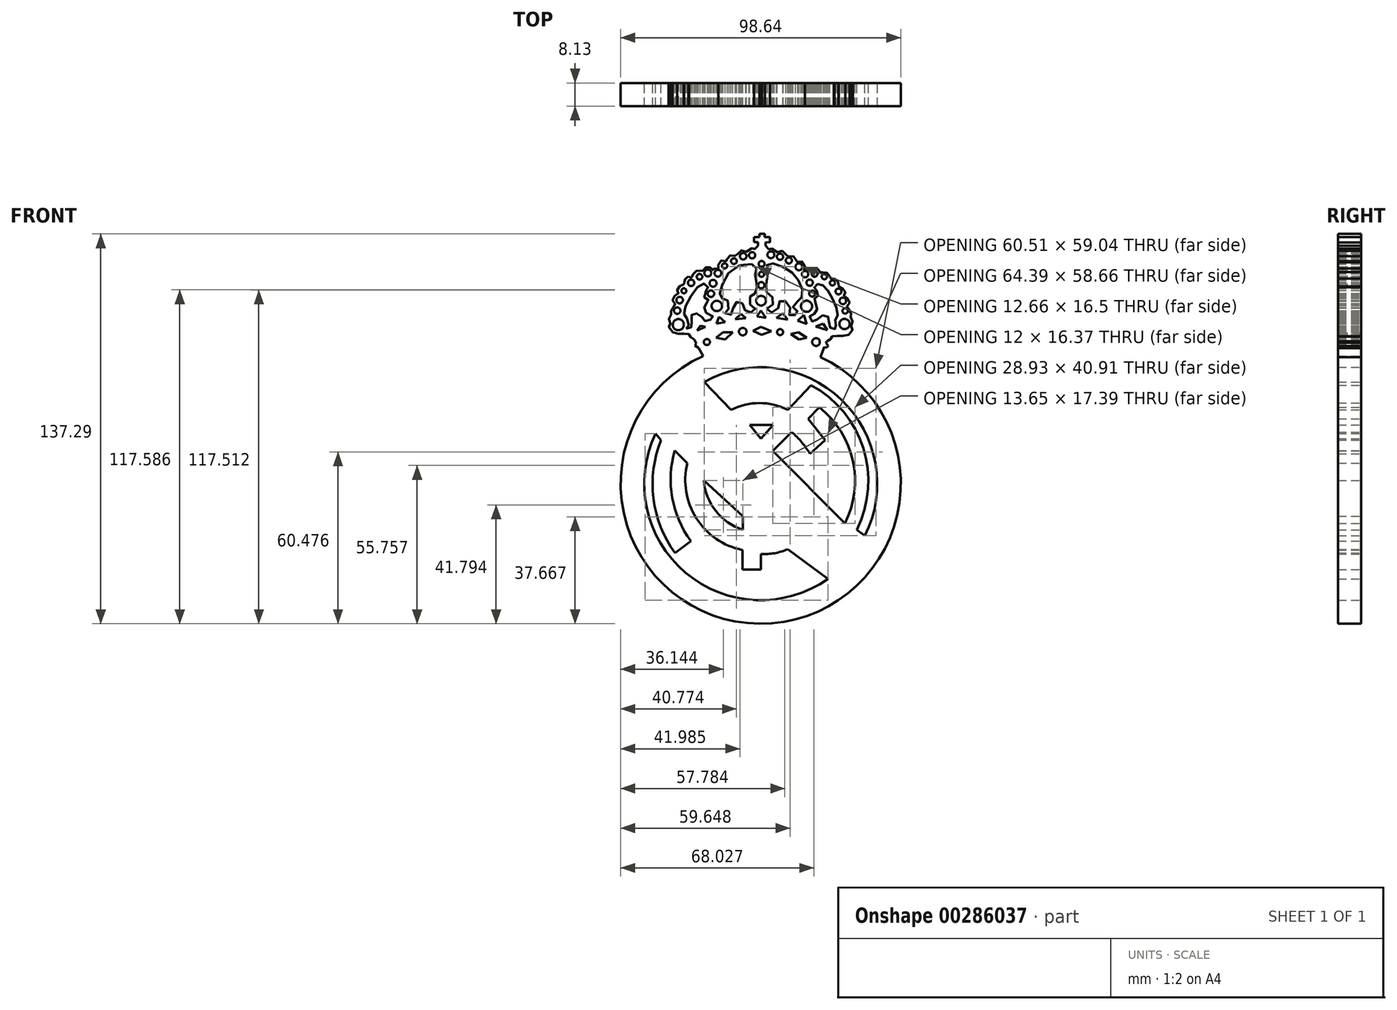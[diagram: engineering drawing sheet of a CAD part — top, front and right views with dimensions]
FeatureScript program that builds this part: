
annotation { "Feature Type Name" : "Feature", "Feature Type Description" : "" }
export const myFeature = defineFeature(function(context is Context, id is Id, definition is map)
    precondition{}
    {
        {
            var Q0;
            Q0=qCreatedBy(makeId("Front.planeOp"),FACE);
            var sketch = newSketch(context, id + "F0", { "sketchPlane" : qUnion([Q0])});
            skCircle(sketch, "E0", {"center": v(0, -1.17) * mm, "radius": 49.32 * mm});
            skCircle(sketch, "E1", {"center": v(0, -1.17) * mm, "radius": 41.02 * mm});
            skArc(sketch, "E2", {"start": v(-18.95, 33.67) * mm, "mid": v(-37.34, 6.45) * mm, "end": v(-30.16, -25.6) * mm});
            skArc(sketch, "E3", {"start": v(-19.8, 27.48) * mm, "mid": v(-31.53, 3.97) * mm, "end": v(-24.63, -21.38) * mm});
            skLineSegment(sketch, "E4", {"start": v(-19.8, 27.48) * mm, "end": v(-14.73, 21.41) * mm});
            skLineSegment(sketch, "E5", {"start": v(-18.95, 33.67) * mm, "end": v(-10.43, 24.82) * mm});
            skArc(sketch, "E6", {"start": v(-14.73, 21.41) * mm, "mid": v(-26.18, -4.34) * mm, "end": v(-6.47, -24.5) * mm});
            skLineSegment(sketch, "E7", {"start": v(-6.47, -24.5) * mm, "end": v(-6.47, -31.38) * mm});
            skLineSegment(sketch, "E8", {"start": v(-6.47, -31.38) * mm, "end": v(0, -31.38) * mm});
            skLineSegment(sketch, "E9", {"start": v(0, -31.38) * mm, "end": v(0, -25.92) * mm});
            skArc(sketch, "E10", {"start": v(0, -25.92) * mm, "mid": v(10.77, -23.7) * mm, "end": v(19, -16.42) * mm});
            skLineSegment(sketch, "E11", {"start": v(19, -16.42) * mm, "end": v(15.77, -12.98) * mm});
            skArc(sketch, "E12", {"start": v(0, -19.42) * mm, "mid": v(8.55, -17.84) * mm, "end": v(15.77, -12.98) * mm});
            skLineSegment(sketch, "E13", {"start": v(0, -19.42) * mm, "end": v(0, -13.17) * mm});
            skLineSegment(sketch, "E14", {"start": v(0, -13.17) * mm, "end": v(7.9, -13.17) * mm});
            skLineSegment(sketch, "E15", {"start": v(7.9, -13.17) * mm, "end": v(7.9, -8.88) * mm});
            skLineSegment(sketch, "E16", {"start": v(7.9, -8.88) * mm, "end": v(0, -8.88) * mm});
            skLineSegment(sketch, "E17", {"start": v(0, -8.88) * mm, "end": v(0, -3.61) * mm});
            skLineSegment(sketch, "E18", {"start": v(0, -3.61) * mm, "end": v(8.16, -3.61) * mm});
            skLineSegment(sketch, "E19", {"start": v(8.16, -3.61) * mm, "end": v(8.16, 0.94) * mm});
            skLineSegment(sketch, "E20", {"start": v(8.16, 0.94) * mm, "end": v(-6.35, 0.94) * mm});
            skLineSegment(sketch, "E21", {"start": v(-6.35, 0.94) * mm, "end": v(-6.35, -17.53) * mm});
            skArc(sketch, "E22", {"start": v(-11.49, 17.79) * mm, "mid": v(-19.81, -1.63) * mm, "end": v(-5.9, -17.53) * mm});
            skLineSegment(sketch, "E23", {"start": v(-11.49, 17.79) * mm, "end": v(0, 6.2) * mm});
            skLineSegment(sketch, "E24", {"start": v(0, 6.2) * mm, "end": v(10.89, 17) * mm});
            skArc(sketch, "E25", {"start": v(17.4, 9.33) * mm, "mid": v(14.45, 13.43) * mm, "end": v(10.89, 17) * mm});
            skLineSegment(sketch, "E26", {"start": v(17.4, 9.33) * mm, "end": v(22.73, 14.2) * mm});
            skLineSegment(sketch, "E27", {"start": v(22.73, 14.2) * mm, "end": v(16.74, 21.7) * mm});
            skLineSegment(sketch, "E28", {"start": v(16.74, 21.7) * mm, "end": v(20.65, 25.72) * mm});
            skLineSegment(sketch, "E29", {"start": v(-4.2, 19.87) * mm, "end": v(0, 14.73) * mm});
            skLineSegment(sketch, "E30", {"start": v(0, 14.73) * mm, "end": v(4.38, 19.54) * mm});
            skLineSegment(sketch, "E31", {"start": v(4.38, 19.54) * mm, "end": v(-3.94, 19.54) * mm});
            skArc(sketch, "E32", {"start": v(9.56, 24.82) * mm, "mid": v(-0.44, 27.23) * mm, "end": v(-10.43, 24.82) * mm});
            skLineSegment(sketch, "E33", {"start": v(9.56, 24.82) * mm, "end": v(17.72, 33.54) * mm});
            skArc(sketch, "E34", {"start": v(30.1, -23.34) * mm, "mid": v(36.99, 7.94) * mm, "end": v(17.72, 33.54) * mm});
            skLineSegment(sketch, "E35", {"start": v(30.1, -24) * mm, "end": v(26.4, -20.38) * mm});
            skLineSegment(sketch, "E36", {"start": v(30.1, -24) * mm, "end": v(30.1, -23.34) * mm});
            skArc(sketch, "E37", {"start": v(26.4, -20.38) * mm, "mid": v(32.95, 3.85) * mm, "end": v(20.65, 25.72) * mm});
            skLineSegment(sketch, "E38", {"start": v(-23.41, 49.61) * mm, "end": v(-20.3, 43.78) * mm});
            skArc(sketch, "E39", {"start": v(23.39, 49.61) * mm, "mid": v(-0.01, 54.78) * mm, "end": v(-23.41, 49.61) * mm});
            skLineSegment(sketch, "E40", {"start": v(23.39, 49.61) * mm, "end": v(21, 43.45) * mm});
            skCircle(sketch, "E41", {"center": v(-6.34, 52.39) * mm, "radius": 1.32 * mm});
            skCircle(sketch, "E42", {"center": v(6.84, 52.21) * mm, "radius": 1.06 * mm});
            skCircle(sketch, "E43", {"center": v(19.47, 48.72) * mm, "radius": 1.36 * mm});
            skCircle(sketch, "E44", {"center": v(-18.96, 48.72) * mm, "radius": 1.07 * mm});
            skLineSegment(sketch, "E45", {"start": v(-15.7, 50.27) * mm, "end": v(-13.28, 52.16) * mm});
            skLineSegment(sketch, "E46", {"start": v(-13.28, 52.16) * mm, "end": v(-9.81, 52.16) * mm});
            skLineSegment(sketch, "E47", {"start": v(-9.81, 52.16) * mm, "end": v(-12.48, 49.66) * mm});
            skLineSegment(sketch, "E48", {"start": v(-12.48, 49.66) * mm, "end": v(-15.7, 50.27) * mm});
            skLineSegment(sketch, "E49", {"start": v(-2.79, 52.65) * mm, "end": v(0, 54) * mm});
            skLineSegment(sketch, "E50", {"start": v(0, 54) * mm, "end": v(3.69, 52.55) * mm});
            skLineSegment(sketch, "E51", {"start": v(3.69, 52.55) * mm, "end": v(0.37, 51.28) * mm});
            skLineSegment(sketch, "E52", {"start": v(0.37, 51.28) * mm, "end": v(-2.79, 52.65) * mm});
            skLineSegment(sketch, "E53", {"start": v(10.66, 51.51) * mm, "end": v(13.3, 52.2) * mm});
            skLineSegment(sketch, "E54", {"start": v(13.3, 52.2) * mm, "end": v(16.15, 50.27) * mm});
            skLineSegment(sketch, "E55", {"start": v(16.15, 50.27) * mm, "end": v(13.51, 49.6) * mm});
            skLineSegment(sketch, "E56", {"start": v(13.51, 49.6) * mm, "end": v(10.66, 51.51) * mm});
            skLineSegment(sketch, "E57", {"start": v(21.74, 47.98) * mm, "end": v(22.72, 48.74) * mm});
            skLineSegment(sketch, "E58", {"start": v(22.72, 48.74) * mm, "end": v(23.77, 47.39) * mm});
            skLineSegment(sketch, "E59", {"start": v(23.77, 47.39) * mm, "end": v(22.77, 46.6) * mm});
            skLineSegment(sketch, "E60", {"start": v(22.77, 46.6) * mm, "end": v(21.74, 47.98) * mm});
            skLineSegment(sketch, "E61", {"start": v(-23.17, 47.48) * mm, "end": v(-22.33, 48.72) * mm});
            skLineSegment(sketch, "E62", {"start": v(-22.33, 48.72) * mm, "end": v(-21.23, 47.98) * mm});
            skLineSegment(sketch, "E63", {"start": v(-21.23, 47.98) * mm, "end": v(-21.85, 46.7) * mm});
            skLineSegment(sketch, "E64", {"start": v(-21.85, 46.7) * mm, "end": v(-23.17, 47.48) * mm});
            skFitSpline(sketch, "E65", {"points": [v(-23.41, 49.61) * mm, v(-24.63, 50.25) * mm, v(-24.83, 51.38) * mm, v(-26.15, 51.41) * mm, v(-27.74, 51.82) * mm, v(-29.91, 51.63) * mm, v(-31.74, 52.96) * mm, v(-32.4, 54.69) * mm, v(-31.7, 55.44) * mm, v(-32.37, 57.27) * mm, v(-31.39, 58.64) * mm, v(-31.58, 59.61) * mm, v(-31.25, 60.68) * mm, v(-30, 61.73) * mm, v(-30.35, 62.4) * mm, v(-31, 63.53) * mm, v(-30.36, 64.92) * mm, v(-29.07, 65.58) * mm, v(-29.1, 66.47) * mm, v(-29.42, 67.18) * mm, v(-28.47, 68.4) * mm, v(-27.42, 69.04) * mm, v(-27.31, 68.9) * mm, v(-27.11, 68.87) * mm, v(-27.02, 68.87) * mm, v(-27.07, 69.37) * mm, v(-27.04, 69.57) * mm, v(-26.93, 69.92) * mm, v(-26.85, 70.13) * mm, v(-26.72, 70.73) * mm, v(-26.55, 71) * mm, v(-26.24, 71.27) * mm, v(-26.14, 71.33) * mm, v(-25.83, 71.55) * mm, v(-25.5, 71.78) * mm, v(-25.46, 71.78) * mm], "startDerivative": vector(-42.62, 10.47) * mm, "endDerivative": vector(5.76, -0.88) * mm});
            skFitSpline(sketch, "E66", {"points": [v(-25.2, 71.6) * mm, v(-25, 71.53) * mm, v(-24.31, 71.49) * mm, v(-23.83, 72.47) * mm, v(-22.74, 73.75) * mm, v(-21.4, 73.87) * mm, v(-20.68, 73.53) * mm, v(-19.78, 74.75) * mm, v(-18.21, 75.08) * mm, v(-17.09, 74.48) * mm, v(-16.74, 73.92) * mm, v(-16.14, 74.72) * mm, v(-14.76, 74.54) * mm, v(-14.86, 76.46) * mm, v(-13.07, 77.5) * mm, v(-11.92, 77.2) * mm, v(-11.57, 78.58) * mm, v(-10.18, 79.29) * mm, v(-8.42, 79.14) * mm, v(-7.47, 80.76) * mm, v(-5.47, 80.74) * mm, v(-4.95, 80.38) * mm, v(-4.16, 81.2) * mm, v(-2.84, 81.66) * mm, v(-2.29, 81.4) * mm, v(-0.9, 82.66) * mm, v(-1.03, 82.88) * mm], "startDerivative": vector(9.59, -4.45) * mm, "endDerivative": vector(-13, 8.44) * mm});
            skLineSegment(sketch, "E67", {"start": v(0.46, 86.8) * mm, "end": v(-0.49, 86.8) * mm});
            skLineSegment(sketch, "E68", {"start": v(-0.49, 86.8) * mm, "end": v(-0.49, 85.74) * mm});
            skLineSegment(sketch, "E69", {"start": v(-0.49, 85.74) * mm, "end": v(-2.4, 85.74) * mm});
            skLineSegment(sketch, "E70", {"start": v(-2.4, 85.74) * mm, "end": v(-2.4, 83.88) * mm});
            skLineSegment(sketch, "E71", {"start": v(-2.4, 83.88) * mm, "end": v(-0.9, 83.88) * mm});
            skLineSegment(sketch, "E72", {"start": v(-0.9, 83.88) * mm, "end": v(-0.9, 82.66) * mm});
            skFitSpline(sketch, "E73.MirrorCS", {"points": [v(23.28, 48.95) * mm, v(24.5, 49.56) * mm, v(24.75, 50.67) * mm, v(26.07, 50.67) * mm, v(27.67, 51.03) * mm, v(29.83, 50.79) * mm, v(31.7, 52.06) * mm, v(32.4, 53.77) * mm, v(31.73, 54.54) * mm, v(32.45, 56.35) * mm, v(31.5, 57.75) * mm, v(31.73, 58.72) * mm, v(31.43, 59.8) * mm, v(30.2, 60.88) * mm, v(30.58, 61.53) * mm, v(31.26, 62.65) * mm, v(30.66, 64.06) * mm, v(29.38, 64.75) * mm, v(29.45, 65.64) * mm, v(29.78, 66.34) * mm, v(28.87, 67.6) * mm, v(27.84, 68.26) * mm, v(27.72, 68.12) * mm, v(27.52, 68.1) * mm, v(27.43, 68.1) * mm, v(27.49, 68.6) * mm, v(27.47, 68.8) * mm, v(27.37, 69.15) * mm, v(27.3, 69.36) * mm, v(27.18, 69.97) * mm, v(27.02, 70.24) * mm, v(26.71, 70.52) * mm, v(26.62, 70.58) * mm, v(26.31, 70.82) * mm, v(26, 71.05) * mm, v(25.95, 71.05) * mm], "startDerivative": vector(42.9, 9.26) * mm, "endDerivative": vector(-5.78, -0.72) * mm});
            skFitSpline(sketch, "E74.MirrorCS", {"points": [v(25.69, 70.89) * mm, v(25.48, 70.81) * mm, v(24.8, 70.79) * mm, v(24.34, 71.79) * mm, v(23.3, 73.1) * mm, v(21.95, 73.25) * mm, v(21.23, 72.94) * mm, v(20.36, 74.18) * mm, v(18.8, 74.56) * mm, v(17.66, 74) * mm, v(17.3, 73.44) * mm, v(16.72, 74.25) * mm, v(15.34, 74.11) * mm, v(15.49, 76.03) * mm, v(13.73, 77.13) * mm, v(12.57, 76.86) * mm, v(12.26, 78.24) * mm, v(10.9, 79) * mm, v(9.13, 78.9) * mm, v(8.22, 80.54) * mm, v(6.23, 80.57) * mm, v(5.7, 80.23) * mm, v(4.93, 81.07) * mm, v(3.63, 81.56) * mm, v(3.06, 81.33) * mm, v(1.72, 82.63) * mm, v(1.85, 82.84) * mm], "startDerivative": vector(-9.7, -4.18) * mm, "endDerivative": vector(13.23, 8.07) * mm});
            skLineSegment(sketch, "E75.MirrorCS", {"start": v(3.3, 85.66) * mm, "end": v(3.24, 83.8) * mm});
            skLineSegment(sketch, "E76.MirrorCS", {"start": v(1.75, 83.84) * mm, "end": v(1.72, 82.63) * mm});
            skLineSegment(sketch, "E77.MirrorCS", {"start": v(3.24, 83.8) * mm, "end": v(1.75, 83.84) * mm});
            skLineSegment(sketch, "E78.MirrorCS", {"start": v(1.39, 85.72) * mm, "end": v(3.3, 85.66) * mm});
            skLineSegment(sketch, "E79.MirrorCS", {"start": v(1.42, 86.78) * mm, "end": v(1.39, 85.72) * mm});
            skLineSegment(sketch, "E80.MirrorCS", {"start": v(0.46, 86.8) * mm, "end": v(1.42, 86.78) * mm});
            skCircle(sketch, "E81", {"center": v(-29, 54.84) * mm, "radius": 1.96 * mm});
            skCircle(sketch, "E82", {"center": v(-29.4, 59.77) * mm, "radius": 1.1 * mm});
            skCircle(sketch, "E83", {"center": v(-28.54, 63.5) * mm, "radius": 1.16 * mm});
            skCircle(sketch, "E84", {"center": v(-27.05, 66.77) * mm, "radius": 0.87 * mm});
            skCircle(sketch, "E85", {"center": v(-24.52, 69.58) * mm, "radius": 1.13 * mm});
            skCircle(sketch, "E86", {"center": v(-21.54, 71.7) * mm, "radius": 0.98 * mm});
            skCircle(sketch, "E87", {"center": v(-18.62, 73.02) * mm, "radius": 1.22 * mm});
            skCircle(sketch, "E88", {"center": v(-15.06, 72.96) * mm, "radius": 1.2 * mm});
            skCircle(sketch, "E89", {"center": v(-12.7, 75.54) * mm, "radius": 0.92 * mm});
            skCircle(sketch, "E90", {"center": v(-9.44, 77.2) * mm, "radius": 1 * mm});
            skCircle(sketch, "E91", {"center": v(-6.17, 78.93) * mm, "radius": 1.15 * mm});
            skCircle(sketch, "E92", {"center": v(-3.02, 79.27) * mm, "radius": 1.1 * mm});
            skCircle(sketch, "E93", {"center": v(-16.78, 69.4) * mm, "radius": 1.22 * mm});
            skCircle(sketch, "E94", {"center": v(-17.53, 65.73) * mm, "radius": 1.15 * mm});
            skCircle(sketch, "E95", {"center": v(-15.46, 61.43) * mm, "radius": 1.84 * mm});
            skCircle(sketch, "E96", {"center": v(0.13, 63.27) * mm, "radius": 1.7 * mm});
            skCircle(sketch, "E97", {"center": v(0.2, 68.72) * mm, "radius": 1.11 * mm});
            skCircle(sketch, "E98", {"center": v(0.26, 72.56) * mm, "radius": 0.9 * mm});
            skCircle(sketch, "E99", {"center": v(0.31, 76.23) * mm, "radius": 1.02 * mm});
            skCircle(sketch, "E100", {"center": v(16.14, 61.32) * mm, "radius": 1.96 * mm});
            skCircle(sketch, "E101", {"center": v(18.15, 65.8) * mm, "radius": 1.06 * mm});
            skCircle(sketch, "E102", {"center": v(17.23, 69.63) * mm, "radius": 1.11 * mm});
            skCircle(sketch, "E103", {"center": v(29.5, 55.07) * mm, "radius": 1.8 * mm});
            skCircle(sketch, "E104", {"center": v(29.73, 59.66) * mm, "radius": 0.95 * mm});
            skCircle(sketch, "E105", {"center": v(28.93, 63.21) * mm, "radius": 1.16 * mm});
            skCircle(sketch, "E106", {"center": v(27.38, 66.54) * mm, "radius": 1.03 * mm});
            skCircle(sketch, "E107", {"center": v(25.26, 69.52) * mm, "radius": 0.9 * mm});
            skCircle(sketch, "E108", {"center": v(22.4, 71.76) * mm, "radius": 0.94 * mm});
            skCircle(sketch, "E109", {"center": v(18.95, 72.73) * mm, "radius": 1.02 * mm});
            skCircle(sketch, "E110", {"center": v(3.58, 79.44) * mm, "radius": 1.2 * mm});
            skCircle(sketch, "E111", {"center": v(6.8, 78.75) * mm, "radius": 1.1 * mm});
            skCircle(sketch, "E112", {"center": v(9.89, 77.43) * mm, "radius": 1.08 * mm});
            skCircle(sketch, "E113", {"center": v(13.44, 75.2) * mm, "radius": 1.22 * mm});
            skFitSpline(sketch, "E114", {"points": [v(-26.19, 53.46) * mm, v(-24.4, 54.03) * mm, v(-24.4, 56.84) * mm, v(-23.9, 58.74) * mm, v(-21.14, 58.1) * mm, v(-19.88, 56.27) * mm, v(-18.39, 56.27) * mm, v(-16.67, 57.42) * mm, v(-19.65, 59.37) * mm, v(-19.76, 61.43) * mm, v(-19.02, 62.4) * mm, v(-18.44, 63.5) * mm, v(-19.76, 64.36) * mm, v(-19.07, 67.05) * mm, v(-18.56, 68.03) * mm, v(-20, 69.23) * mm, v(-24, 65.8) * mm, v(-27.05, 59.14) * mm, v(-26.07, 57.19) * mm, v(-25.44, 54.44) * mm, v(-26.19, 53.46) * mm]});
            skFitSpline(sketch, "E115", {"points": [v(-12.54, 58.9) * mm, v(-10.99, 58.16) * mm, v(-9.84, 59.66) * mm, v(-9.38, 61.9) * mm, v(-7.66, 63.04) * mm, v(-6.23, 61.95) * mm, v(-5.37, 59.77) * mm, v(-3.82, 59.02) * mm, v(-1.75, 60.11) * mm, v(-3.07, 61.03) * mm, v(-3.93, 63.15) * mm, v(-3.3, 65.33) * mm, v(-1.93, 65.85) * mm, v(-1.3, 67.63) * mm, v(-1.47, 69.92) * mm, v(-1.87, 71.13) * mm, v(-1.93, 73.08) * mm, v(-1.52, 74.8) * mm, v(-2.9, 76.06) * mm, v(-9.73, 74.62) * mm, v(-13.68, 68.32) * mm, v(-14.37, 65.28) * mm, v(-13.74, 64.07) * mm, v(-12.3, 64.01) * mm, v(-11.16, 61.66) * mm, v(-12.08, 59.25) * mm, v(-12.54, 58.9) * mm]});
            skFitSpline(sketch, "E116", {"points": [v(2.15, 60.46) * mm, v(3.75, 59.14) * mm, v(6.23, 60.8) * mm, v(6.68, 63.1) * mm, v(8.63, 63.1) * mm, v(10.35, 60.52) * mm, v(10.12, 58.16) * mm, v(11.95, 58.22) * mm, v(13.16, 59.25) * mm, v(11.38, 60.63) * mm, v(12.3, 62.4) * mm, v(13.96, 63.9) * mm, v(14.82, 65.9) * mm, v(13.16, 70.78) * mm, v(9.49, 74.28) * mm, v(3.8, 76.4) * mm, v(2.2, 75.77) * mm, v(2.49, 72.04) * mm, v(1.86, 66.7) * mm, v(3.87, 64.82) * mm, v(4.33, 62) * mm, v(2.15, 60.46) * mm]});
            skFitSpline(sketch, "E117", {"points": [v(19.98, 69.12) * mm, v(18.84, 67.86) * mm, v(19.75, 66.77) * mm, v(20.04, 64.82) * mm, v(18.84, 63.9) * mm, v(19.47, 62.12) * mm, v(19.52, 59.02) * mm, v(17.17, 57.75) * mm, v(18.43, 55.87) * mm, v(21.02, 57.75) * mm, v(23.65, 57.75) * mm, v(24.11, 54.84) * mm, v(24.75, 53.58) * mm, v(26.64, 53.58) * mm, v(26.07, 55.98) * mm, v(26.98, 57.75) * mm, v(25.6, 63.27) * mm, v(22.62, 68.03) * mm, v(19.98, 69.12) * mm]});
            skCircle(sketch, "E118", {"center": v(15.62, 72.62) * mm, "radius": 1.11 * mm});
            skLineSegment(sketch, "E119", {"start": v(-22.4, 52.77) * mm, "end": v(-21.23, 54.45) * mm});
            skLineSegment(sketch, "E120", {"start": v(-21.23, 54.45) * mm, "end": v(-19.47, 54.03) * mm});
            skLineSegment(sketch, "E121", {"start": v(-19.47, 54.03) * mm, "end": v(-22.4, 52.77) * mm});
            skLineSegment(sketch, "E122", {"start": v(-15.52, 55.24) * mm, "end": v(-14.67, 57.65) * mm});
            skLineSegment(sketch, "E123", {"start": v(-14.67, 57.65) * mm, "end": v(-12.48, 55.7) * mm});
            skLineSegment(sketch, "E124", {"start": v(-12.48, 55.7) * mm, "end": v(-15.52, 55.24) * mm});
            skLineSegment(sketch, "E125", {"start": v(-8.92, 56.73) * mm, "end": v(-6.86, 58.68) * mm});
            skLineSegment(sketch, "E126", {"start": v(-6.86, 58.68) * mm, "end": v(-5.33, 57.06) * mm});
            skLineSegment(sketch, "E127", {"start": v(-5.33, 57.06) * mm, "end": v(-8.92, 56.73) * mm});
            skLineSegment(sketch, "E128", {"start": v(5.46, 57.23) * mm, "end": v(7.83, 58.91) * mm});
            skLineSegment(sketch, "E129", {"start": v(7.83, 58.91) * mm, "end": v(9.52, 56.54) * mm});
            skLineSegment(sketch, "E130", {"start": v(9.52, 56.54) * mm, "end": v(5.46, 57.23) * mm});
            skLineSegment(sketch, "E131", {"start": v(13.07, 56.27) * mm, "end": v(15.2, 58.23) * mm});
            skLineSegment(sketch, "E132", {"start": v(15.2, 58.23) * mm, "end": v(16.2, 55.14) * mm});
            skLineSegment(sketch, "E133", {"start": v(16.2, 55.14) * mm, "end": v(13.38, 56.14) * mm});
            skLineSegment(sketch, "E134", {"start": v(13.38, 56.14) * mm, "end": v(13.07, 56.27) * mm});
            skLineSegment(sketch, "E135", {"start": v(-1.34, 57.77) * mm, "end": v(0.08, 59.83) * mm});
            skLineSegment(sketch, "E136", {"start": v(0.08, 59.83) * mm, "end": v(1.84, 57.23) * mm});
            skLineSegment(sketch, "E137", {"start": v(1.84, 57.23) * mm, "end": v(-1.34, 57.77) * mm});
            skLineSegment(sketch, "E138", {"start": v(19.37, 54.2) * mm, "end": v(22.04, 55.15) * mm});
            skLineSegment(sketch, "E139", {"start": v(22.04, 55.15) * mm, "end": v(23.37, 52.96) * mm});
            skLineSegment(sketch, "E140", {"start": v(23.37, 52.96) * mm, "end": v(19.37, 54.2) * mm});
            skLineSegment(sketch, "E141", {"start": v(4.73, 9.92) * mm, "end": v(28.45, -13.98) * mm});
            skLineSegment(sketch, "E142", {"start": v(28.45, -13.98) * mm, "end": v(29.65, -15.19) * mm});
            skLineSegment(sketch, "E143", {"start": v(30.6, -25.47) * mm, "end": v(30.1, -24) * mm});
            skLineSegment(sketch, "E144", {"start": v(-30.3, 10.47) * mm, "end": v(-25.87, 6.01) * mm});
            skLineSegment(sketch, "E145", {"start": v(-20, 0) * mm, "end": v(-6.35, -12.56) * mm});
            skLineSegment(sketch, "E146", {"start": v(23.28, 48.95) * mm, "end": v(23.13, 48.94) * mm});
            skLineSegment(sketch, "E147", {"start": v(-25.46, 71.78) * mm, "end": v(-25.2, 71.6) * mm});
            skLineSegment(sketch, "E148", {"start": v(25.69, 70.89) * mm, "end": v(25.95, 71.05) * mm});
            skLineSegment(sketch, "E149", {"start": v(4.73, 9.92) * mm, "end": v(4.24, 10.42) * mm});
            skLineSegment(sketch, "E150", {"start": v(-30.16, -25.6) * mm, "end": v(-24.63, -21.38) * mm});
            skLineSegment(sketch, "E151", {"start": v(30.6, -25.47) * mm, "end": v(32.02, -26.8) * mm});
            skLineSegment(sketch, "E152", {"start": v(-35.07, 14.2) * mm, "end": v(-37.01, 16.5) * mm});
            skLineSegment(sketch, "E153", {"start": v(-18.95, 33.67) * mm, "end": v(-19.92, 34.68) * mm});
            skLineSegment(sketch, "E154", {"start": v(10.77, -25.15) * mm, "end": v(23.65, -34.7) * mm});
            skPoint(sketch, "E154.startSnap0", {"position": v(10.77, -23.7) * mm});
            skLineSegment(sketch, "E155", {"start": v(10.77, -25.15) * mm, "end": v(9.57, -24.26) * mm});
            skLineSegment(sketch, "E156", {"start": v(33.8, -17.39) * mm, "end": v(36.68, -19.53) * mm});
            skSolve(sketch);
        }
        {
            var Q0;
            Q0=qSketchRegion(id+"F0",true);
            var Q1;
            {var subQ10=sQuery(id+"F0.wireOp",EDGE,"E11");Q1=makeQuery(id+"F0.imprint","IMPRINT",FACE,{"disambiguationData":[TD([[makeQuery(id+"F0.imprint","IMPRINT",EDGE,{"derivedFrom":subQ10}),-1.0]])]});}
            var Q2;
            {var subQ13=sQuery(id+"F0.wireOp",EDGE,"E4");Q2=makeQuery(id+"F0.imprint","IMPRINT",FACE,{"disambiguationData":[TD([[makeQuery(id+"F0.imprint","IMPRINT",EDGE,{"derivedFrom":subQ13}),1.0]])]});}
            var Q3;
            {var subQ0=sQuery(id+"F0.wireOp",EDGE,"E4");Q3=makeQuery(id+"F0.imprint","IMPRINT",FACE,{"disambiguationData":[TD([[makeQuery(id+"F0.imprint","IMPRINT",EDGE,{"derivedFrom":subQ0}),-1.0]])]});}
            var Q4;
            {var subQ0=sQuery(id+"F0.wireOp",EDGE,"E152");Q4=makeQuery(id+"F0.imprint","IMPRINT",FACE,{"disambiguationData":[TD([[makeQuery(id+"F0.imprint","IMPRINT",EDGE,{"derivedFrom":subQ0}),-1.0]])]});}
            var Q5;
            {var subQ0=sQuery(id+"F0.wireOp",EDGE,"E36");Q5=makeQuery(id+"F0.imprint","IMPRINT",FACE,{"disambiguationData":[TD([[makeQuery(id+"F0.imprint","IMPRINT",EDGE,{"derivedFrom":subQ0}),-1.0]])]});}
            extrude(context, id + "F1", {"entities" : qUnion([Q0, Q1, Q2, Q3, Q4, Q5]), "depth" : 8.13 * mm});
        }
    });
